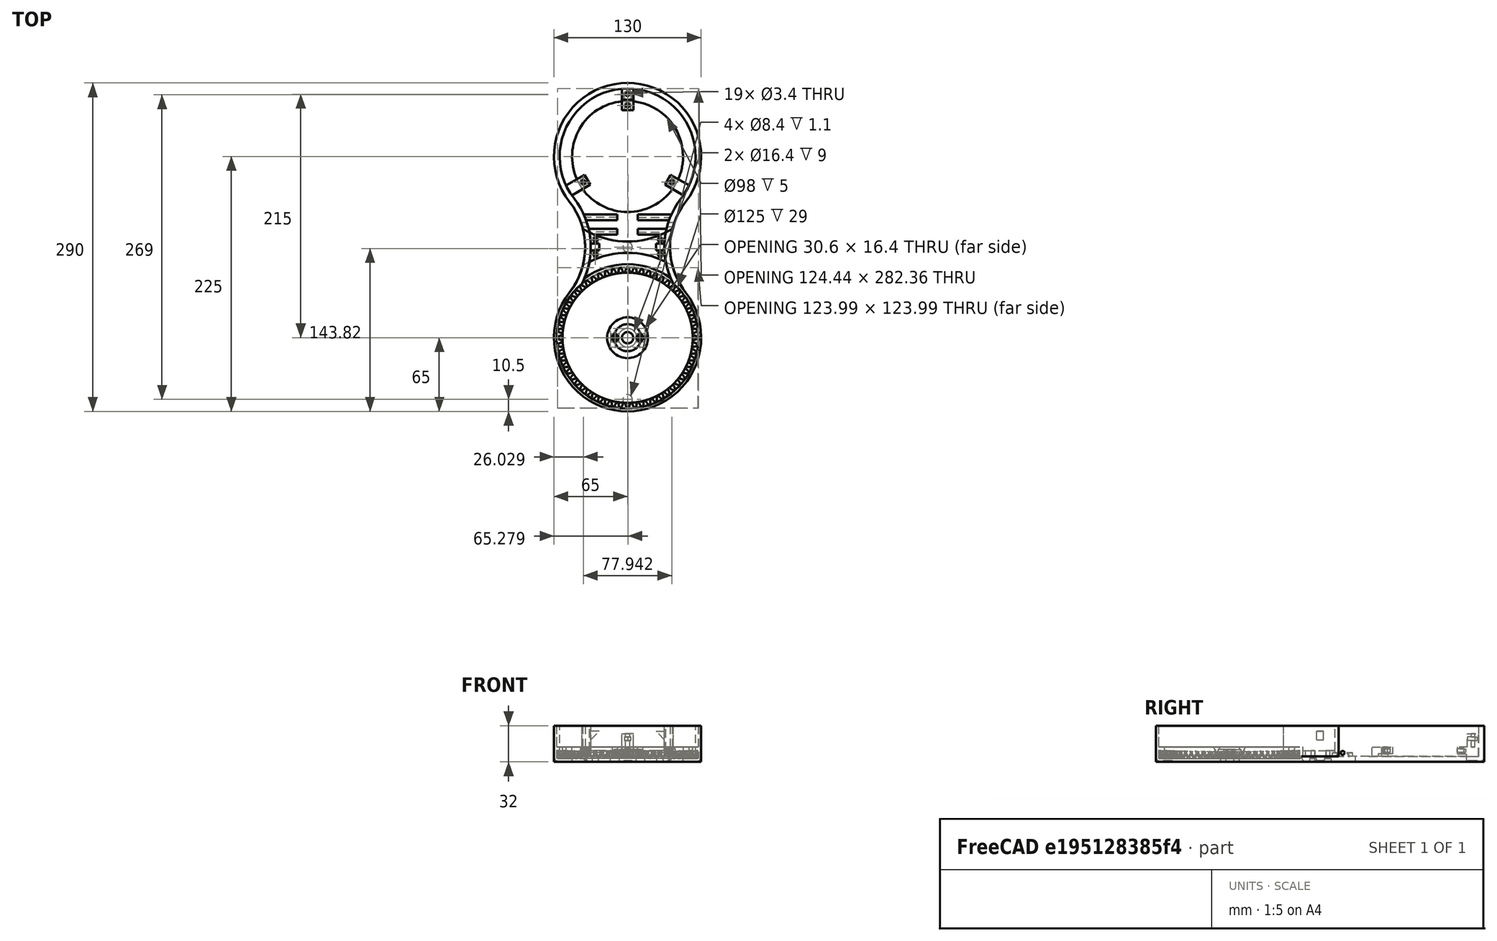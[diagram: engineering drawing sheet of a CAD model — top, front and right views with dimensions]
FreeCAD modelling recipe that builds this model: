
FCSTD DOCUMENT  (FreeCAD 0.19R24276 (Git))
Label: Art2BodyA_Splitted_A
License: All rights reserved
LicenseURL: http://en.wikipedia.org/wiki/All_rights_reserved
objects: Sketcher::SketchObject×25, PartDesign::Pocket×17, PartDesign::Line×11, PartDesign::CoordinateSystem×10, PartDesign::Pad×8, PartDesign::Plane×4, PartDesign::Body×3, PartDesign::FeatureBase×2, Spreadsheet::Sheet×1, Part::FeaturePython×1, Part::Cylinder×1, Part::Cut×1, Part::MultiFuse×1, PartDesign::Chamfer×1, PartDesign::Mirrored×1, PartDesign::PolarPattern×1, PartDesign::Fillet×1, Part::Feature×1
note: 116 computed .brp shape members not serialized (recipe doc carries the construction recipe); baked Part::Feature solids carry a one-line shape summary decoded from their .brp

FEATURE [Spreadsheet::Sheet] Spreadsheet
  cells = A2=M3BoltBodyRadius; B2(M3BoltBodyRadius)=1.7; A3=M3BoltHeadRadius; B3(M3BoltHeadRadius)=2.95; A4=M3NutCircumradius; B4(M3NutCircumradius)=3.35; A5=M3NutThickness; B5(M3NutThickness)=3; A6=Bearing655ZZBodyRadius; B6(Bearing655ZZBodyRadius)=8.199999999999999; A7=MagnetRadius; B7(MagnetRadius)=4.2; A8=MagnetThickness; B8(MagnetThickness)=1.1
FEATURE [Sketcher::SketchObject] Sketch
  FullyConstrained = true
  MapMode = 5
  Support = -> [XY_Plane]
  sketch-geometry (4):
    g0: ArcOfCircle CenterX=0 CenterY=0 CenterZ=0 NormalX=0 NormalY=0 NormalZ=1 AngleXU=0 Radius=65 StartAngle=2.47872 EndAngle=6.94606
    g1: ArcOfCircle CenterX=102.47 CenterY=80 CenterZ=0 NormalX=0 NormalY=0 NormalZ=1 AngleXU=0 Radius=65 StartAngle=2.47872 EndAngle=3.80447
    g2: ArcOfCircle CenterX=-102.47 CenterY=80 CenterZ=0 NormalX=0 NormalY=0 NormalZ=1 AngleXU=0 Radius=65 StartAngle=5.62031 EndAngle=6.94606
    g3: ArcOfCircle CenterX=2.8e-15 CenterY=160 CenterZ=0 NormalX=0 NormalY=0 NormalZ=1 AngleXU=0 Radius=65 StartAngle=5.62031 EndAngle=10.0877
  constraints (10):
    c: Coincident(g0,g-1)
    c: Tangent(g2,g0) = 1.5708
    c: Tangent(g1,g0) = 1.5708
    c: Symmetric(g1,g2,g-2)
    c: Tangent(g3,g1) = 1.5708
    c: Tangent(g3,g2) = 1.5708
    c: Equal(g3,g0)
    c: DistanceY(g0,g3) = 160
    c: Radius(g0) = 65
    c: Equal(g2,g0)
FEATURE [PartDesign::Pad] Pad
  Direction = (1,1,1)
  Length = 32
  Length2 = 100
  Profile = -> Sketch
  Refine = true
  Type = 0
FEATURE [Sketcher::SketchObject] Sketch001
  ExternalGeometry = -> [Pad]
  FullyConstrained = true
  MapMode = 5
  Placement = pos=(0,0,32) rot=(0,0,1;0rad)
  Support = -> [Pad]
  sketch-geometry (4):
    g0: ArcOfCircle CenterX=0 CenterY=0 CenterZ=0 NormalX=0 NormalY=0 NormalZ=1 AngleXU=0 Radius=60 StartAngle=2.47872 EndAngle=6.94606
    g1: ArcOfCircle CenterX=102.47 CenterY=80 CenterZ=0 NormalX=0 NormalY=0 NormalZ=1 AngleXU=0 Radius=70 StartAngle=2.47872 EndAngle=3.80447
    g2: ArcOfCircle CenterX=-102.47 CenterY=80 CenterZ=0 NormalX=0 NormalY=0 NormalZ=1 AngleXU=0 Radius=70 StartAngle=5.62031 EndAngle=6.94606
    g3: ArcOfCircle CenterX=2.7e-15 CenterY=160 CenterZ=0 NormalX=0 NormalY=0 NormalZ=1 AngleXU=0 Radius=60 StartAngle=5.62031 EndAngle=10.0877
  constraints (9):
    c: Coincident(g0,g-1)
    c: Coincident(g1,g-4)
    c: Coincident(g2,g-5)
    c: Coincident(g2,g0)
    c: Coincident(g3,g-3)
    c: Tangent(g3,g2) = 1.5708
    c: Radius(g3) = 60
    c: Tangent(g3,g1) = 1.5708
    c: Tangent(g1,g0) = 1.5708
FEATURE [PartDesign::Pocket] Pocket
  BaseFeature = -> Pad
  Length = 27
  Length2 = 100
  Profile = -> Sketch001
  Refine = true
  Type = 0
FEATURE [Part::FeaturePython] involutegear  # WARN: FeaturePython — macro-defined, semantics opaque (R4)
  Placement = pos=(0,0,3) rot=(0,0,1;0rad)
  backlash = 0
  beta = -32
  clearance = 0.25
  double_helix = false
  dw = 120
  head = 0
  height = 15.5
  module = 2
  numpoints = 6
  pressure_angle = 20
  properties_from_tool = false
  reversed_backlash = false
  shift = 0
  simple = false
  teeth = 60
  transverse_pitch = 6.28319
  undercut = false
  version = 0.0.3
FEATURE [Sketcher::SketchObject] Sketch003
  FullyConstrained = true
  MapMode = 5
  Placement = pos=(0,0,3) rot=(0,0,1;0rad)
  sketch-geometry (1):
    g0: Circle CenterX=0 CenterY=0 CenterZ=0 NormalX=0 NormalY=0 NormalZ=1 AngleXU=0 Radius=18
  constraints (2):
    c: Coincident(g0,g-1)
    c: Radius(g0) = 18
FEATURE [PartDesign::Plane] DatumPlane
  AttachmentOffset = pos=(0,0,9) rot=(0,0,1;0rad)
  Length = 315.452
  MapMode = 5
  Placement = pos=(9,-2e-15,2e-15) rot=(0.57735,0.57735,0.57735;2.0944rad)
  ResizeMode = 0
  Support = -> [YZ_Plane001]
  Width = 82.7027
FEATURE [PartDesign::CoordinateSystem] LCS_Art2BodyA
  AttacherType = Attacher::AttachEngine3D
FEATURE [Part::Cylinder] Cylinder
  Angle = 360
  AttacherType = Attacher::AttachEngine3D
  Height = 13
  Radius = 64.9
FEATURE [Sketcher::SketchObject] Sketch021
  FullyConstrained = true
  MapMode = 5
  Placement = pos=(0,0,32) rot=(0,0,1;0rad)
  Support = -> [Pocket]
  sketch-geometry (1):
    g0: Circle CenterX=0 CenterY=0 CenterZ=0 NormalX=0 NormalY=0 NormalZ=1 AngleXU=0 Radius=62.5
  constraints (2):
    c: Coincident(g0,g-1)
    c: Radius(g0) = 62.5
FEATURE [PartDesign::Pocket] Pocket014
  BaseFeature = -> Pocket
  Length = 29
  Length2 = 100
  Profile = -> Sketch021
  Refine = true
  Type = 0
FEATURE [PartDesign::Body] Body
  Group = -> [Sketch,Pad,Sketch001,Pocket,Sketch021,Pocket014]
  Origin = -> Origin
  Tip = -> Pocket014
FEATURE [PartDesign::Plane] DatumPlane003
  AttachmentOffset = pos=(0,0,-80) rot=(0,0,1;0rad)
  Length = 147.174
  MapMode = 5
  Placement = pos=(0,80,1.78e-14) rot=(1,0,0;1.5708rad)
  ResizeMode = 0
  Support = -> [XZ_Plane001]
  Width = 74.2136
FEATURE [Part::Cut] Cut
  Base = -> Cylinder
  Refine = true
  Tool = -> involutegear
FEATURE [Part::MultiFuse] Fusion
  Refine = true
  Shapes = -> [Cut,Pocket014]
FEATURE [PartDesign::FeatureBase] BaseFeature  label="Fusion001"
  BaseFeature = -> Fusion
FEATURE [PartDesign::Pad] Pad002
  BaseFeature = -> BaseFeature
  Direction = (1,1,1)
  Length = 8
  Length2 = 100
  Profile = -> Sketch003
  Refine = true
  Type = 0
FEATURE [PartDesign::Chamfer] Chamfer
  Angle = 45
  Base = -> Pad002 [Edge755]
  BaseFeature = -> Pad002
  ChamferType = 0
  FlipDirection = false
  Refine = true
  Size = 6
  Size2 = 1
  SupportTransform = false
FEATURE [Sketcher::SketchObject] Sketch004
  FullyConstrained = true
  MapMode = 5
  Placement = pos=(0,0,11) rot=(0,0,1;0rad)
  Support = -> [Chamfer]
  expr: Constraints[5] = Spreadsheet.M3BoltBodyRadius
  sketch-geometry (3):
    g0: Circle CenterX=0 CenterY=0 CenterZ=0 NormalX=0 NormalY=0 NormalZ=1 AngleXU=0 Radius=5
    g1: Circle CenterX=11 CenterY=0 CenterZ=0 NormalX=0 NormalY=0 NormalZ=1 AngleXU=0 Radius=1.7
    g2: Circle CenterX=-11 CenterY=0 CenterZ=0 NormalX=0 NormalY=0 NormalZ=1 AngleXU=0 Radius=1.7
  constraints (7):
    c: Coincident(g0,g-1)
    c: PointOnObject(g1,g-1)
    c: Symmetric(g2,g1,g-2)
    c: DistanceX(g2,g1) = 22
    c: Radius(g0) = 5
    c: Radius(g2) = 1.7
    c: Equal(g1,g2)
FEATURE [PartDesign::Pocket] Pocket001
  BaseFeature = -> Chamfer
  Length = 5
  Length2 = 100
  Profile = -> Sketch004
  Refine = true
  Type = 1
FEATURE [Sketcher::SketchObject] Sketch005
  FullyConstrained = true
  MapMode = 5
  Placement = pos=(0,0,0) rot=(1,0,0;3.14159rad)
  Support = -> [Pocket001]
  expr: Constraints[1] = Spreadsheet.Bearing655ZZBodyRadius
  sketch-geometry (1):
    g0: Circle CenterX=0 CenterY=0 CenterZ=0 NormalX=0 NormalY=0 NormalZ=1 AngleXU=0 Radius=8.2
  constraints (2):
    c: Coincident(g0,g-1)
    c: Radius(g0) = 8.2
FEATURE [PartDesign::Pocket] Pocket002
  BaseFeature = -> Pocket001
  Length = 9
  Length2 = 100
  Profile = -> Sketch005
  Refine = true
  Type = 0
FEATURE [Sketcher::SketchObject] Sketch006
  FullyConstrained = true
  MapMode = 5
  Placement = pos=(0,0,0) rot=(1,0,0;3.14159rad)
  Support = -> [Pocket002]
  sketch-geometry (4):
    g0: LineSegment StartX=-15.3 StartY=3.5 StartZ=0 EndX=15.3 EndY=3.5 EndZ=0
    g1: LineSegment StartX=15.3 StartY=3.5 StartZ=0 EndX=15.3 EndY=-3.5 EndZ=0
    g2: LineSegment StartX=15.3 StartY=-3.5 StartZ=0 EndX=-15.3 EndY=-3.5 EndZ=0
    g3: LineSegment StartX=-15.3 StartY=-3.5 StartZ=0 EndX=-15.3 EndY=3.5 EndZ=0
  constraints (10):
    c: Coincident(g0,g1)
    c: Coincident(g1,g2)
    c: Coincident(g2,g3)
    c: Coincident(g3,g0)
    c: Horizontal(g0)
    c: Vertical(g3)
    c: Symmetric(g0,g1,g-1)
    c: Symmetric(g2,g1,g-2)
    c: DistanceX(g2,g2) = 30.6
    c: DistanceY(g3,g3) = 7
FEATURE [PartDesign::Pocket] Pocket003
  BaseFeature = -> Pocket002
  Length = 4
  Length2 = 100
  Profile = -> Sketch006
  Refine = true
  Type = 0
FEATURE [Sketcher::SketchObject] Sketch007
  ExternalGeometry = -> [Pocket003]
  FullyConstrained = true
  MapMode = 5
  Placement = pos=(0,0,11) rot=(0,0,1;0rad)
  Support = -> [Pocket003]
  expr: Constraints[39] = Spreadsheet.M3NutCircumradius
  sketch-geometry (14):
    g0: LineSegment StartX=11 StartY=3.35 StartZ=0 EndX=8.09881 EndY=1.675 EndZ=0
    g1: LineSegment StartX=8.09881 StartY=1.675 StartZ=0 EndX=8.09881 EndY=-1.675 EndZ=0
    g2: LineSegment StartX=8.09881 StartY=-1.675 StartZ=0 EndX=11 EndY=-3.35 EndZ=0
    g3: LineSegment StartX=11 StartY=-3.35 StartZ=0 EndX=13.9012 EndY=-1.675 EndZ=0
    g4: LineSegment StartX=13.9012 StartY=-1.675 StartZ=0 EndX=13.9012 EndY=1.675 EndZ=0
    g5: LineSegment StartX=13.9012 StartY=1.675 StartZ=0 EndX=11 EndY=3.35 EndZ=0
    g6: Circle CenterX=11 CenterY=0 CenterZ=0 NormalX=0 NormalY=0 NormalZ=1 AngleXU=0 Radius=3.35
    g7: LineSegment StartX=-11 StartY=3.35 StartZ=0 EndX=-13.9012 EndY=1.675 EndZ=0
    g8: LineSegment StartX=-13.9012 StartY=1.675 StartZ=0 EndX=-13.9012 EndY=-1.675 EndZ=0
    g9: LineSegment StartX=-13.9012 StartY=-1.675 StartZ=0 EndX=-11 EndY=-3.35 EndZ=0
    g10: LineSegment StartX=-11 StartY=-3.35 StartZ=0 EndX=-8.09881 EndY=-1.675 EndZ=0
    g11: LineSegment StartX=-8.09881 StartY=-1.675 StartZ=0 EndX=-8.09881 EndY=1.675 EndZ=0
    g12: LineSegment StartX=-8.09881 StartY=1.675 StartZ=0 EndX=-11 EndY=3.35 EndZ=0
    g13: Circle CenterX=-11 CenterY=0 CenterZ=0 NormalX=0 NormalY=0 NormalZ=1 AngleXU=0 Radius=3.35
  constraints (32):
    c: Coincident(g0,g1)
    c: Coincident(g1,g2)
    c: Coincident(g2,g3)
    c: Coincident(g3,g4)
    c: Coincident(g4,g5)
    c: Coincident(g5,g0)
    c: Equal(g0, g1-g5) x5
    c: PointOnObject(g0,g6)
    c: PointOnObject(g1,g6)
    c: PointOnObject(g2,g6)
    c: PointOnObject(g3,g6)
    c: PointOnObject(g4,g6)
    c: PointOnObject(g5,g6)
    c: Coincident(g6,g-3)
    c: Coincident(g7,g8)
    c: Coincident(g8,g9)
    c: Coincident(g9,g10)
    c: Coincident(g10,g11)
    c: Coincident(g11,g12)
    c: Coincident(g12,g7)
    c: Equal(g7, g8-g12) x5
    c: PointOnObject(g7,g13)
    c: PointOnObject(g8,g13)
    c: PointOnObject(g9,g13)
    c: PointOnObject(g10,g13)
    c: PointOnObject(g11,g13)
    c: PointOnObject(g12,g13)
    c: Coincident(g13,g-4)
    c: Vertical(g11)
    c: Vertical(g1)
    c: Equal(g6,g13)
    c: Radius(g6) = 3.35
FEATURE [PartDesign::Pocket] Pocket004
  BaseFeature = -> Pocket003
  Length = 4
  Length2 = 100
  Profile = -> Sketch007
  Refine = true
  Type = 0
FEATURE [Sketcher::SketchObject] Sketch008
  ExternalGeometry = -> [Pocket004]
  FullyConstrained = true
  MapMode = 5
  Placement = pos=(0,0,0) rot=(1,0,0;3.14159rad)
  Support = -> [Pocket004]
  sketch-geometry (1):
    g0: Circle CenterX=0 CenterY=-160 CenterZ=0 NormalX=0 NormalY=0 NormalZ=1 AngleXU=0 Radius=49
  constraints (2):
    c: Radius(g0) = 49
    c: Coincident(g0,g-3)
FEATURE [PartDesign::Pocket] Pocket005
  BaseFeature = -> Pocket004
  Length = 5
  Length2 = 100
  Profile = -> Sketch008
  Refine = true
  Type = 0
FEATURE [Sketcher::SketchObject] Sketch009
  ExternalGeometry = -> [Pocket005]
  FullyConstrained = true
  MapMode = 5
  Placement = pos=(0,0,5) rot=(0,0,1;0rad)
  Support = -> [Pocket005]
  sketch-geometry (4):
    g0: ArcOfCircle CenterX=0 CenterY=0 CenterZ=0 NormalX=0 NormalY=0 NormalZ=1 AngleXU=0 Radius=75 StartAngle=1.10499 EndAngle=2.0366
    g1: ArcOfCircle CenterX=2.7e-15 CenterY=160 CenterZ=0 NormalX=0 NormalY=0 NormalZ=1 AngleXU=0 Radius=75 StartAngle=4.24659 EndAngle=5.17819
    g2: ArcOfCircle CenterX=102.47 CenterY=80 CenterZ=0 NormalX=0 NormalY=0 NormalZ=1 AngleXU=0 Radius=70 StartAngle=2.95493 EndAngle=3.32825
    g3: ArcOfCircle CenterX=-102.47 CenterY=80 CenterZ=0 NormalX=0 NormalY=0 NormalZ=1 AngleXU=0 Radius=70 StartAngle=6.09653 EndAngle=6.46984
  constraints (12):
    c: Coincident(g0,g-1)
    c: Radius(g0) = 75
    c: Coincident(g2,g1)
    c: Coincident(g2,g0)
    c: Coincident(g3,g1)
    c: Coincident(g3,g0)
    c: Equal(g1,g0)
    c: Coincident(g1,g-3)
    c: Equal(g3,g2)
    c: Coincident(g2,g-4)
    c: Coincident(g3,g-5)
    c: Equal(g3,g-5)
FEATURE [PartDesign::Pad] Pad003
  BaseFeature = -> Pocket005
  Direction = (1,1,1)
  Length = 5
  Length2 = 100
  Profile = -> Sketch009
  Refine = true
  Type = 0
FEATURE [Sketcher::SketchObject] Sketch010
  ExternalGeometry = -> [Pad003]
  FullyConstrained = true
  MapMode = 5
  Placement = pos=(9,-2e-15,2e-15) rot=(0.57735,0.57735,0.57735;2.0944rad)
  Support = -> [DatumPlane]
  sketch-geometry (8):
    g0: LineSegment StartX=91 StartY=8.03897 StartZ=0 EndX=96 EndY=8.03897 EndZ=0
    g1: LineSegment StartX=96 StartY=8.03897 StartZ=0 EndX=93.45 EndY=5 EndZ=0
    g2: LineSegment StartX=93.45 StartY=5 StartZ=0 EndX=91 EndY=5 EndZ=0
    g3: LineSegment StartX=91 StartY=5 StartZ=0 EndX=91 EndY=8.03897 EndZ=0
    g4: LineSegment StartX=103.7 StartY=8.03897 StartZ=0 EndX=108.7 EndY=8.03897 EndZ=0
    g5: LineSegment StartX=108.7 StartY=8.03897 StartZ=0 EndX=108.7 EndY=5 EndZ=0
    g6: LineSegment StartX=108.7 StartY=5 StartZ=0 EndX=106.25 EndY=5 EndZ=0
    g7: LineSegment StartX=106.25 StartY=5 StartZ=0 EndX=103.7 EndY=8.03897 EndZ=0
  constraints (24):
    c: Horizontal(g0)
    c: Coincident(g0,g1)
    c: PointOnObject(g1,g-3)
    c: Coincident(g1,g2)
    c: Horizontal(g2)
    c: Coincident(g2,g3)
    c: Vertical(g3)
    c: Coincident(g0,g3)
    c: Horizontal(g4)
    c: Coincident(g4,g5)
    c: Vertical(g5)
    c: Coincident(g5,g6)
    c: Horizontal(g6)
    c: Coincident(g6,g7)
    c: Coincident(g7,g4)
    c: Equal(g1,g7)
    c: Equal(g5,g3)
    c: Equal(g4,g0)
    c: PointOnObject(g6,g-3)
    c: DistanceX(g1,g6) = 12.8
    c: DistanceX(g0,g4) = 7.7
    c: Angle(g-3,g1) = 0.872665
    c: DistanceX(g0,g0) = 5
    c: DistanceX(g-1,g2) = 91
FEATURE [PartDesign::Pad] Pad004
  BaseFeature = -> Pad003
  Direction = (1,1,1)
  Length = 10
  Length2 = 100
  Profile = -> Sketch010
  Refine = true
  Type = 3
  UpToFace = -> Pad003 [Face265]
FEATURE [PartDesign::Mirrored] Mirrored
  BaseFeature = -> Pad004
  MirrorPlane = -> YZ_Plane001
  Originals = -> [Pad004]
  Refine = true
FEATURE [Sketcher::SketchObject] Sketch011
  ExternalGeometry = -> [Mirrored]
  FullyConstrained = true
  MapMode = 5
  Placement = pos=(0,0,0) rot=(0.57735,0.57735,0.57735;2.0944rad)
  Support = -> [YZ_Plane001]
  sketch-geometry (6):
    g0: LineSegment StartX=221 StartY=5 StartZ=0 EndX=221 EndY=13 EndZ=0
    g1: LineSegment StartX=221 StartY=13 StartZ=0 EndX=201 EndY=13 EndZ=0
    g2: LineSegment StartX=201 StartY=13 StartZ=0 EndX=201 EndY=7 EndZ=0
    g3: LineSegment StartX=201 StartY=7 StartZ=0 EndX=209 EndY=7 EndZ=0
    g4: LineSegment StartX=209 StartY=7 StartZ=0 EndX=209 EndY=5 EndZ=0
    g5: LineSegment StartX=209 StartY=5 StartZ=0 EndX=221 EndY=5 EndZ=0
  constraints (17):
    c: Vertical(g0)
    c: Coincident(g0,g1)
    c: Coincident(g1,g2)
    c: Coincident(g2,g3)
    c: Coincident(g3,g4)
    c: Coincident(g4,g5)
    c: Coincident(g5,g0)
    c: Horizontal(g5)
    c: Vertical(g4)
    c: Vertical(g2)
    c: Horizontal(g3)
    c: Horizontal(g1)
    c: DistanceX(g3,g3) = 8
    c: DistanceX(g1,g1) = 20
    c: DistanceY(g2,g2) = 6
    c: DistanceY(g4,g4) = 2
    c: Coincident(g4,g-3)
FEATURE [PartDesign::Pad] Pad005
  BaseFeature = -> Mirrored
  Direction = (1,1,1)
  Length = 10
  Length2 = 100
  Midplane = true
  Profile = -> Sketch011
  Refine = true
  Type = 0
FEATURE [Sketcher::SketchObject] Sketch012
  ExternalGeometry = -> [Pad005]
  FullyConstrained = false
  MapMode = 5
  Placement = pos=(-3.6e-15,2.9e-15,13) rot=(0,0,1;0rad)
  Support = -> [Pad005]
  expr: Constraints[1] = Spreadsheet.M3BoltBodyRadius
  sketch-geometry (1):
    g0: Circle CenterX=0 CenterY=205 CenterZ=0 NormalX=0 NormalY=0 NormalZ=1 AngleXU=0 Radius=1.7
  constraints (2):
    c: PointOnObject(g0,g-2)
    c: Radius(g0) = 1.7
FEATURE [PartDesign::Pocket] Pocket006
  BaseFeature = -> Pad005
  Length = 5
  Length2 = 100
  Profile = -> Sketch012
  Refine = true
  Type = 1
FEATURE [PartDesign::Plane] DatumPlane001
  AttachmentOffset = pos=(0,0,-3) rot=(0,0,1;0rad)
  Length = 168.771
  MapMode = 5
  Placement = pos=(-2.8e-15,2.2e-15,10) rot=(0,0,1;0rad)
  ResizeMode = 0
  Support = -> [Pocket006]
  Width = 328.56
FEATURE [Sketcher::SketchObject] Sketch013
  ExternalGeometry = -> [Pocket006]
  FullyConstrained = true
  MapMode = 5
  Placement = pos=(-2.8e-15,2.2e-15,10) rot=(0,0,1;0rad)
  Support = -> [DatumPlane001]
  expr: Constraints[18] = Spreadsheet.M3NutCircumradius
  sketch-geometry (10):
    g0: LineSegment StartX=0 StartY=208.35 StartZ=0 EndX=-2.90119 EndY=206.675 EndZ=0
    g1: LineSegment StartX=-2.90119 StartY=206.675 StartZ=0 EndX=-2.90119 EndY=203.325 EndZ=0
    g2: LineSegment StartX=-2.90119 StartY=203.325 StartZ=0 EndX=-9.28e-14 EndY=201.65 EndZ=0
    g3: LineSegment StartX=-9.28e-14 StartY=201.65 StartZ=0 EndX=2.90119 EndY=203.325 EndZ=0
    g4: LineSegment StartX=2.90119 StartY=203.325 StartZ=0 EndX=2.90119 EndY=206.675 EndZ=0
    g5: LineSegment StartX=2.90119 StartY=206.675 StartZ=0 EndX=0 EndY=208.35 EndZ=0
    g6: Circle CenterX=0 CenterY=205 CenterZ=0 NormalX=0 NormalY=0 NormalZ=1 AngleXU=0 Radius=3.35
    g7: LineSegment StartX=-2.90119 StartY=206.675 StartZ=0 EndX=-2.90119 EndY=196.675 EndZ=0
    g8: LineSegment StartX=-2.90119 StartY=196.675 StartZ=0 EndX=2.90119 EndY=196.675 EndZ=0
    g9: LineSegment StartX=2.90119 StartY=196.675 StartZ=0 EndX=2.90119 EndY=206.675 EndZ=0
  constraints (24):
    c: Coincident(g0,g1)
    c: Coincident(g1,g2)
    c: Coincident(g2,g3)
    c: Coincident(g3,g4)
    c: Coincident(g4,g5)
    c: Coincident(g5,g0)
    c: Equal(g0, g1-g5) x5
    c: PointOnObject(g0,g6)
    c: PointOnObject(g1,g6)
    c: PointOnObject(g2,g6)
    c: PointOnObject(g3,g6)
    c: PointOnObject(g4,g6)
    c: PointOnObject(g5,g6)
    c: PointOnObject(g5,g-2)
    c: Radius(g6) = 3.35
    c: Coincident(g0,g7)
    c: Vertical(g7)
    c: Coincident(g7,g8)
    c: Horizontal(g8)
    c: Coincident(g8,g9)
    c: Coincident(g9,g5)
    c: Vertical(g9)
    c: DistanceY(g9,g9) = 10
    c: Coincident(g6,g-3)
FEATURE [PartDesign::Pocket] Pocket007
  BaseFeature = -> Pocket006
  Length = 3
  Length2 = 100
  Midplane = true
  Profile = -> Sketch013
  Refine = true
  Type = 0
  expr: Length = Spreadsheet.M3NutThickness
FEATURE [PartDesign::Line] DatumLine
  AttacherType = Attacher::AttachEngineLine
  Length = 20
  MapMode = 19
  Placement = pos=(-7.1e-15,160,0) rot=(-1,0,0;3.14159rad)
  ResizeMode = 0
  Support = -> [Pocket007]
FEATURE [PartDesign::PolarPattern] PolarPattern
  Angle = 360
  Axis = -> DatumLine
  BaseFeature = -> Pocket007
  Occurrences = 3
  Originals = -> [Pad005,Pocket006,Pocket007]
  Refine = true
FEATURE [Sketcher::SketchObject] Sketch014
  ExternalGeometry = -> [PolarPattern]
  FullyConstrained = true
  MapMode = 5
  Placement = pos=(-3.6e-15,2.9e-15,13) rot=(0,0,1;0rad)
  Support = -> [PolarPattern]
  sketch-geometry (4):
    g0: LineSegment StartX=-5 StartY=219.791 StartZ=0 EndX=-5 EndY=210 EndZ=0
    g1: LineSegment StartX=-5 StartY=210 StartZ=0 EndX=5 EndY=210 EndZ=0
    g2: LineSegment StartX=5 StartY=210 StartZ=0 EndX=5 EndY=219.791 EndZ=0
    g3: ArcOfCircle CenterX=1.16e-14 CenterY=160 CenterZ=0 NormalX=0 NormalY=0 NormalZ=1 AngleXU=0 Radius=60 StartAngle=1.48737 EndAngle=1.65423
  constraints (11):
    c: Vertical(g0)
    c: Coincident(g0,g1)
    c: Coincident(g1,g2)
    c: Vertical(g2)
    c: Symmetric(g1,g0,g-2)
    c: Coincident(g3,g0)
    c: Coincident(g3,g2)
    c: DistanceY(g-4,g1) = 9
    c: Coincident(g3,g-3)
    c: Equal(g-3,g3)
    c: DistanceX(g1,g1) = 10
FEATURE [PartDesign::Pad] Pad006
  BaseFeature = -> PolarPattern
  Direction = (1,1,1)
  Length = 12
  Length2 = 100
  Profile = -> Sketch014
  Refine = true
  Type = 0
FEATURE [Sketcher::SketchObject] Sketch015
  ExternalGeometry = -> [Pad006]
  FullyConstrained = true
  MapMode = 5
  Placement = pos=(-7.3e-15,6.8e-15,25) rot=(0,0,1;0rad)
  Support = -> [Pad006]
  expr: Constraints[1] = Spreadsheet.M3BoltBodyRadius
  sketch-geometry (1):
    g0: Circle CenterX=0 CenterY=215 CenterZ=0 NormalX=0 NormalY=0 NormalZ=1 AngleXU=0 Radius=1.7
  constraints (3):
    c: DistanceY(g-3,g0) = 5
    c: Radius(g0) = 1.7
    c: PointOnObject(g0,g-2)
FEATURE [PartDesign::Pocket] Pocket008
  BaseFeature = -> Pad006
  Length = 12
  Length2 = 100
  Profile = -> Sketch015
  Refine = true
  Type = 0
FEATURE [PartDesign::Plane] DatumPlane002
  AttachmentOffset = pos=(0,0,-4.5) rot=(0,0,1;0rad)
  Length = 168.771
  MapMode = 5
  Placement = pos=(-5.9e-15,5.5e-15,20.5) rot=(0,0,1;0rad)
  ResizeMode = 0
  Support = -> [Pocket008]
  Width = 328.56
FEATURE [Sketcher::SketchObject] Sketch016
  ExternalGeometry = -> [Pocket008]
  FullyConstrained = true
  MapMode = 5
  Placement = pos=(-5.9e-15,5.5e-15,20.5) rot=(0,0,1;0rad)
  Support = -> [DatumPlane002]
  expr: Constraints[18] = Spreadsheet.M3NutCircumradius
  sketch-geometry (10):
    g0: LineSegment StartX=0 StartY=211.65 StartZ=0 EndX=2.90119 EndY=213.325 EndZ=0
    g1: LineSegment StartX=2.90119 StartY=213.325 StartZ=0 EndX=2.90119 EndY=216.675 EndZ=0
    g2: LineSegment StartX=2.90119 StartY=216.675 StartZ=0 EndX=6.2e-15 EndY=218.35 EndZ=0
    g3: LineSegment StartX=6.2e-15 StartY=218.35 StartZ=0 EndX=-2.90119 EndY=216.675 EndZ=0
    g4: LineSegment StartX=-2.90119 StartY=216.675 StartZ=0 EndX=-2.90119 EndY=213.325 EndZ=0
    g5: LineSegment StartX=-2.90119 StartY=213.325 StartZ=0 EndX=0 EndY=211.65 EndZ=0
    g6: Circle CenterX=0 CenterY=215 CenterZ=0 NormalX=0 NormalY=0 NormalZ=1 AngleXU=0 Radius=3.35
    g7: LineSegment StartX=2.90119 StartY=216.675 StartZ=0 EndX=2.90119 EndY=206.675 EndZ=0
    g8: LineSegment StartX=2.90119 StartY=206.675 StartZ=0 EndX=-2.90119 EndY=206.675 EndZ=0
    g9: LineSegment StartX=-2.90119 StartY=206.675 StartZ=0 EndX=-2.90119 EndY=216.675 EndZ=0
  constraints (24):
    c: Coincident(g0,g1)
    c: Coincident(g1,g2)
    c: Coincident(g2,g3)
    c: Coincident(g3,g4)
    c: Coincident(g4,g5)
    c: Coincident(g5,g0)
    c: Equal(g0, g1-g5) x5
    c: PointOnObject(g0,g6)
    c: PointOnObject(g1,g6)
    c: PointOnObject(g2,g6)
    c: PointOnObject(g3,g6)
    c: PointOnObject(g4,g6)
    c: PointOnObject(g5,g6)
    c: PointOnObject(g5,g-2)
    c: Radius(g6) = 3.35
    c: Vertical(g7)
    c: Coincident(g7,g8)
    c: Coincident(g8,g9)
    c: Vertical(g9)
    c: Horizontal(g8)
    c: Coincident(g7,g1)
    c: Coincident(g9,g3)
    c: Coincident(g6,g-3)
    c: DistanceY(g7,g7) = 10
FEATURE [PartDesign::Pocket] Pocket009
  BaseFeature = -> Pocket008
  Length = 3
  Length2 = 100
  Midplane = true
  Profile = -> Sketch016
  Refine = true
  Type = 0
  expr: Length = Spreadsheet.M3NutThickness
FEATURE [Sketcher::SketchObject] Sketch017
  ExternalGeometry = -> [Pocket009]
  FullyConstrained = true
  MapMode = 5
  Placement = pos=(0,0,0) rot=(0.57735,0.57735,0.57735;2.0944rad)
  Support = -> [YZ_Plane001]
  expr: Constraints[0] = Spreadsheet.M3BoltBodyRadius
  sketch-geometry (3):
    g0: Circle CenterX=99.85 CenterY=8 CenterZ=0 NormalX=0 NormalY=0 NormalZ=1 AngleXU=0 Radius=1.7
    g1: LineSegment StartX=93.45 StartY=5 StartZ=0 EndX=99.85 EndY=8 EndZ=0
    g2: LineSegment StartX=99.85 StartY=8 StartZ=0 EndX=106.25 EndY=5 EndZ=0
  constraints (7):
    c: Radius(g0) = 1.7
    c: Coincident(g1,g-3)
    c: Coincident(g1,g0)
    c: Coincident(g2,g-4)
    c: Coincident(g0,g2)
    c: Equal(g2,g1)
    c: DistanceY(g1,g0) = 3
FEATURE [PartDesign::Pocket] Pocket010
  BaseFeature = -> Pocket009
  Length = 5
  Length2 = 100
  Midplane = true
  Profile = -> Sketch017
  Refine = true
  Type = 1
FEATURE [Sketcher::SketchObject] Sketch018
  FullyConstrained = true
  MapMode = 5
  Placement = pos=(0,0,0) rot=(1,0,0;3.14159rad)
  Support = -> [Pocket010]
  expr: Constraints[14] = Spreadsheet.M3BoltBodyRadius
  sketch-geometry (8):
    g0: Circle CenterX=-28.5 CenterY=-73.5 CenterZ=0 NormalX=0 NormalY=0 NormalZ=1 AngleXU=0 Radius=1.7
    g1: LineSegment StartX=-28.5 StartY=-73.5 StartZ=0 EndX=28.5 EndY=-73.5 EndZ=0
    g2: LineSegment StartX=28.5 StartY=-73.5 StartZ=0 EndX=28.5 EndY=-86.5 EndZ=0
    g3: LineSegment StartX=28.5 StartY=-86.5 StartZ=0 EndX=-28.5 EndY=-86.5 EndZ=0
    g4: LineSegment StartX=-28.5 StartY=-86.5 StartZ=0 EndX=-28.5 EndY=-73.5 EndZ=0
    g5: Circle CenterX=28.5 CenterY=-73.5 CenterZ=0 NormalX=0 NormalY=0 NormalZ=1 AngleXU=0 Radius=1.7
    g6: Circle CenterX=28.5 CenterY=-86.5 CenterZ=0 NormalX=0 NormalY=0 NormalZ=1 AngleXU=0 Radius=1.7
    g7: Circle CenterX=-28.5 CenterY=-86.5 CenterZ=0 NormalX=0 NormalY=0 NormalZ=1 AngleXU=0 Radius=1.7
  constraints (19):
    c: Coincident(g1,g2)
    c: Coincident(g2,g3)
    c: Coincident(g3,g4)
    c: Coincident(g4,g1)
    c: Horizontal(g1)
    c: Vertical(g2)
    c: Vertical(g4)
    c: Coincident(g1,g0)
    c: Coincident(g5,g1)
    c: Coincident(g6,g2)
    c: Coincident(g7,g3)
    c: Equal(g7,g0)
    c: Equal(g0,g5)
    c: Equal(g5,g6)
    c: Radius(g6) = 1.7
    c: Symmetric(g7,g6,g-2)
    c: DistanceY(g4,g4) = 13
    c: DistanceY(g0,g-1) = 73.5
    c: DistanceX(g3,g3) = 57
FEATURE [PartDesign::Pocket] Pocket011
  BaseFeature = -> Pocket010
  Length = 5
  Length2 = 100
  Profile = -> Sketch018
  Refine = true
  Type = 1
FEATURE [Sketcher::SketchObject] Sketch019
  ExternalGeometry = -> [Pocket011]
  FullyConstrained = true
  MapMode = 5
  Placement = pos=(0,0,0) rot=(1,0,0;3.14159rad)
  Support = -> [Pocket011]
  expr: Constraints[1] = Spreadsheet.M3BoltHeadRadius
  sketch-geometry (4):
    g0: Circle CenterX=-28.5 CenterY=-73.5 CenterZ=0 NormalX=0 NormalY=0 NormalZ=1 AngleXU=0 Radius=2.95
    g1: Circle CenterX=-28.5 CenterY=-86.5 CenterZ=0 NormalX=0 NormalY=0 NormalZ=1 AngleXU=0 Radius=2.95
    g2: Circle CenterX=28.5 CenterY=-73.5 CenterZ=0 NormalX=0 NormalY=0 NormalZ=1 AngleXU=0 Radius=2.95
    g3: Circle CenterX=28.5 CenterY=-86.5 CenterZ=0 NormalX=0 NormalY=0 NormalZ=1 AngleXU=0 Radius=2.95
  constraints (8):
    c: Coincident(g0,g-3)
    c: Radius(g0) = 2.95
    c: Equal(g1,g0)
    c: Coincident(g1,g-4)
    c: Coincident(g2,g-5)
    c: Coincident(g3,g-6)
    c: Equal(g3,g2)
    c: Equal(g2,g0)
FEATURE [PartDesign::Pocket] Pocket012
  BaseFeature = -> Pocket011
  Length = 2.9
  Length2 = 100
  Profile = -> Sketch019
  Refine = true
  Type = 0
FEATURE [PartDesign::Fillet] Fillet
  Base = -> Pocket012 [Edge845,Edge848]
  BaseFeature = -> Pocket012
  Radius = 5
  Refine = true
  SupportTransform = false
FEATURE [Sketcher::SketchObject] Sketch020
  FullyConstrained = true
  MapMode = 5
  Placement = pos=(0,0,0) rot=(1,0,0;3.14159rad)
  Support = -> [Fillet]
  expr: Constraints[8] = Spreadsheet.MagnetRadius
  sketch-geometry (3):
    g0: Circle CenterX=0 CenterY=54.5 CenterZ=0 NormalX=0 NormalY=0 NormalZ=1 AngleXU=0 Radius=4.2
    g1: Circle CenterX=0 CenterY=-80 CenterZ=0 NormalX=0 NormalY=0 NormalZ=1 AngleXU=0 Radius=4.2
    g2: Circle CenterX=0 CenterY=-214.5 CenterZ=0 NormalX=0 NormalY=0 NormalZ=1 AngleXU=0 Radius=4.2
  constraints (9):
    c: PointOnObject(g0,g-2)
    c: PointOnObject(g1,g-2)
    c: PointOnObject(g2,g-2)
    c: DistanceY(g-1,g0) = 54.5
    c: DistanceY(g1,g-1) = 80
    c: DistanceY(g2,g1) = 134.5
    c: Equal(g2,g1)
    c: Equal(g1,g0)
    c: Radius(g2) = 4.2
FEATURE [PartDesign::Pocket] Pocket013
  BaseFeature = -> Fillet
  Length = 1.1
  Length2 = 100
  Profile = -> Sketch020
  Refine = true
  Type = 0
  expr: Length = Spreadsheet.MagnetThickness
FEATURE [PartDesign::CoordinateSystem] LCS_Bearing
  AttacherType = Attacher::AttachEngine3D
  MapMode = 11
  Placement = pos=(0,0,9) rot=(0,0,1;1.5708rad)
  Support = -> [Pocket013]
FEATURE [PartDesign::CoordinateSystem] LCS_Window
  AttacherType = Attacher::AttachEngine3D
  MapMode = 11
  Placement = pos=(-7.1e-15,160,0) rot=(0.707107,-0.707107,0;3.14159rad)
  Support = -> [Pocket013]
FEATURE [PartDesign::CoordinateSystem] LCS_Magnet2  label="LCS_Magnet"
  AttacherType = Attacher::AttachEngine3D
  MapMode = 11
  Placement = pos=(0,214.5,1.1) rot=(0.707107,-0.707107,0;3.14159rad)
  Support = -> [Pocket013]
FEATURE [PartDesign::CoordinateSystem] LCS_Magnet1
  AttacherType = Attacher::AttachEngine3D
  MapMode = 11
  Placement = pos=(0,80,1.1) rot=(0.707107,-0.707107,0;3.14159rad)
  Support = -> [Pocket013]
FEATURE [PartDesign::CoordinateSystem] LCS_Magnet2001  label="LCS_Magnet2"
  AttacherType = Attacher::AttachEngine3D
  MapMode = 11
  Placement = pos=(0,-54.5,1.1) rot=(0.707107,-0.707107,0;3.14159rad)
  Support = -> [Pocket013]
FEATURE [PartDesign::CoordinateSystem] LCS_Tensioner001
  AttacherType = Attacher::AttachEngine3D
  MapMode = 45
  Placement = pos=(-9,99.85,5) rot=(0,0.707107,0.707107;3.14159rad)
  Support = -> [Pocket013]
FEATURE [PartDesign::CoordinateSystem] LCS_Tensioner1
  AttacherType = Attacher::AttachEngine3D
  MapMode = 45
  Placement = pos=(9,99.85,5) rot=(0,0.707107,0.707107;3.14159rad)
  Support = -> [Pocket013]
FEATURE [PartDesign::CoordinateSystem] LCS_BearingFix
  AttacherType = Attacher::AttachEngine3D
  MapMode = 45
  Placement = pos=(9.3e-15,0,4) rot=(0,0,1;1.5708rad)
  Support = -> [Pocket013]
FEATURE [PartDesign::Line] HoleAxis_1
  AttacherType = Attacher::AttachEngineLine
  Length = 4.79083
  MapMode = 19
  Placement = pos=(-3.1e-15,205,11.5) rot=(0,0,1;0rad)
  ResizeMode = 1
  Support = -> [Pocket013]
FEATURE [PartDesign::Line] HoleAxis_2
  AttacherType = Attacher::AttachEngineLine
  Length = 4.79083
  MapMode = 19
  Placement = pos=(-6.4e-15,215,22) rot=(0,0,1;0rad)
  ResizeMode = 1
  Support = -> [Pocket013]
FEATURE [PartDesign::Line] HoleAxis_3
  AttacherType = Attacher::AttachEngineLine
  Length = 4.79858
  MapMode = 19
  Placement = pos=(-38.9711,137.5,11.5) rot=(0,0,1;2.0944rad)
  ResizeMode = 1
  Support = -> [Pocket013]
FEATURE [PartDesign::Line] HoleAxis_4
  AttacherType = Attacher::AttachEngineLine
  Length = 4.79858
  MapMode = 19
  Placement = pos=(38.9711,137.5,11.5) rot=(0,0,1;4.18879rad)
  ResizeMode = 1
  Support = -> [Pocket013]
FEATURE [PartDesign::Line] HoleAxis_5
  AttacherType = Attacher::AttachEngineLine
  Length = 4.79083
  MapMode = 19
  Placement = pos=(-28.5,86.5,2.9) rot=(-1,0,0;3.14159rad)
  ResizeMode = 1
  Support = -> [Pocket013]
FEATURE [PartDesign::Line] HoleAxis_6
  AttacherType = Attacher::AttachEngineLine
  Length = 4.79083
  MapMode = 19
  Placement = pos=(-28.5,73.5,2.9) rot=(-1,0,0;3.14159rad)
  ResizeMode = 1
  Support = -> [Pocket013]
FEATURE [PartDesign::Line] HoleAxis_7
  AttacherType = Attacher::AttachEngineLine
  Length = 4.79083
  MapMode = 19
  Placement = pos=(28.5,73.5,2.9) rot=(-1,0,0;3.14159rad)
  ResizeMode = 1
  Support = -> [Pocket013]
FEATURE [PartDesign::Line] HoleAxis_8
  AttacherType = Attacher::AttachEngineLine
  Length = 4.79083
  MapMode = 19
  Placement = pos=(28.5,86.5,2.9) rot=(-1,0,0;3.14159rad)
  ResizeMode = 1
  Support = -> [Pocket013]
FEATURE [PartDesign::Line] HoleAxis_9
  AttacherType = Attacher::AttachEngineLine
  Length = 4.79083
  MapMode = 19
  Placement = pos=(11,0,7) rot=(0,0,1;0rad)
  ResizeMode = 1
  Support = -> [Pocket013]
FEATURE [PartDesign::Line] HoleAxis_10
  AttacherType = Attacher::AttachEngineLine
  Length = 4.79083
  MapMode = 19
  Placement = pos=(-11,0,7) rot=(0,0,1;0rad)
  ResizeMode = 1
  Support = -> [Pocket013]
FEATURE [PartDesign::CoordinateSystem] LCS_Cover
  AttacherType = Attacher::AttachEngine3D
  AttachmentOffset = pos=(0,0,-32) rot=(0,0,1;0rad)
  MapMode = 11
  Placement = pos=(-7.1e-15,160,32) rot=(0.707107,-0.707107,0;3.14159rad)
  Support = -> [Pocket013]
FEATURE [Sketcher::SketchObject] Sketch022
  ExternalGeometry = -> [Pocket013]
  FullyConstrained = true
  MapMode = 5
  Placement = pos=(0,80,1.78e-14) rot=(1,0,0;1.5708rad)
  Support = -> [DatumPlane003]
  sketch-geometry (6):
    g0: LineSegment StartX=-25 StartY=27 StartZ=0 EndX=-35 EndY=27 EndZ=0
    g1: LineSegment StartX=-35 StartY=27 StartZ=0 EndX=-35 EndY=17 EndZ=0
    g2: LineSegment StartX=-35 StartY=17 StartZ=0 EndX=-25 EndY=27 EndZ=0
    g3: LineSegment StartX=25 StartY=27 StartZ=0 EndX=35 EndY=27 EndZ=0
    g4: LineSegment StartX=35 StartY=27 StartZ=0 EndX=35 EndY=17 EndZ=0
    g5: LineSegment StartX=35 StartY=17 StartZ=0 EndX=25 EndY=27 EndZ=0
  constraints (15):
    c: Horizontal(g0)
    c: Coincident(g0,g1)
    c: Vertical(g1)
    c: Coincident(g1,g2)
    c: Coincident(g2,g0)
    c: Coincident(g3,g4)
    c: Coincident(g4,g5)
    c: Coincident(g5,g3)
    c: Symmetric(g3,g0,g-2)
    c: Symmetric(g0,g3,g-2)
    c: Symmetric(g4,g1,g-2)
    c: DistanceX(g0,g3) = 50
    c: DistanceX(g0,g0) = 10
    c: Angle(g0,g2) = 0.785398
    c: DistanceY(g0,g-3) = 5
FEATURE [PartDesign::Pad] Pad007
  BaseFeature = -> Pocket013
  Direction = (1,1,1)
  Length = 6
  Length2 = 100
  Midplane = true
  Profile = -> Sketch022
  Refine = true
  Type = 0
FEATURE [PartDesign::Body] Body001  label="Art2BodyA"
  BaseFeature = -> Fusion
  Group = -> [BaseFeature,Sketch003,Pad002,Chamfer,Sketch004,Pocket001,Sketch005,Pocket002,Sketch006,Pocket003,Sketch007,Pocket004,Sketch008,Pocket005,Sketch009,Pad003,DatumPlane,Sketch010,Pad004,Mirrored,Sketch011,Pad005,Sketch012,Pocket006,DatumPlane001,Sketch013,Pocket007,DatumLine,PolarPattern,Sketch014,Pad006,Sketch015,Pocket008,DatumPlane002,Sketch016,Pocket009,Sketch017,Pocket010,Sketch018,Pocket011,+28 more]
  Origin = -> Origin001
  Tip = -> Pad007
FEATURE [Part::Feature] Body001001  label="Art2BodyA001"
  shape: bbox 139.7 x 299.7 x 32 mm, 392 faces (baked)
FEATURE [PartDesign::FeatureBase] BaseFeature001
  BaseFeature = -> Body001001
FEATURE [Sketcher::SketchObject] Sketch023
  ExternalGeometry = -> [BaseFeature001]
  FullyConstrained = true
  MapMode = 5
  Placement = pos=(0,0,5) rot=(0,0,1;0rad)
  Support = -> [BaseFeature001]
  sketch-geometry (4):
    g0: ArcOfCircle CenterX=0 CenterY=0 CenterZ=0 NormalX=0 NormalY=0 NormalZ=1 AngleXU=0 Radius=64.9 StartAngle=0.94391 EndAngle=2.19768
    g1: ArcOfCircle CenterX=102.47 CenterY=80 CenterZ=0 NormalX=0 NormalY=0 NormalZ=1 AngleXU=0 Radius=70 StartAngle=3.32825 EndAngle=3.5444
    g2: ArcOfCircle CenterX=-102.47 CenterY=80 CenterZ=0 NormalX=0 NormalY=0 NormalZ=1 AngleXU=0 Radius=70 StartAngle=5.88038 EndAngle=6.09653
    g3: ArcOfCircle CenterX=0 CenterY=0 CenterZ=0 NormalX=0 NormalY=0 NormalZ=1 AngleXU=0 Radius=75 StartAngle=1.10499 EndAngle=2.0366
  constraints (11):
    c: Coincident(g0,g-1)
    c: PointOnObject(g0,g-4)
    c: Coincident(g1,g-4)
    c: Coincident(g1,g0)
    c: Coincident(g2,g-5)
    c: Coincident(g2,g0)
    c: Coincident(g2,g-3)
    c: Coincident(g3,g0)
    c: Coincident(g3,g2)
    c: Coincident(g3,g1)
    c: Equal(g-6,g0)
FEATURE [PartDesign::Pad] Pad008
  BaseFeature = -> BaseFeature001
  Direction = (1,1,1)
  Length = 5
  Length2 = 100
  Profile = -> Sketch023
  Refine = true
  Type = 0
FEATURE [Sketcher::SketchObject] Sketch024
  ExternalGeometry = -> [Pad008]
  FullyConstrained = true
  MapMode = 5
  Placement = pos=(0,0,0) rot=(1,0,0;3.14159rad)
  Support = -> [Pad008]
  sketch-geometry (1):
    g0: Circle CenterX=0 CenterY=-160 CenterZ=0 NormalX=0 NormalY=0 NormalZ=1 AngleXU=0 Radius=75
  constraints (2):
    c: Radius(g0) = 75
    c: Coincident(g-3,g0)
FEATURE [PartDesign::Pocket] Pocket015
  BaseFeature = -> Pad008
  Length = 5
  Length2 = 100
  Profile = -> Sketch024
  Refine = true
  Type = 1
FEATURE [Sketcher::SketchObject] Sketch025
  FullyConstrained = true
  MapMode = 5
  Placement = pos=(0,0,0) rot=(1,0,0;3.14159rad)
  Support = -> [Pocket015]
  sketch-geometry (4):
    g0: ArcOfCircle CenterX=0 CenterY=0 CenterZ=0 NormalX=0 NormalY=0 NormalZ=1 AngleXU=0 Radius=75 StartAngle=3.98266 EndAngle=5.44212
    g1: LineSegment StartX=50 StartY=-55.9017 StartZ=0 EndX=50 EndY=-115.902 EndZ=0
    g2: LineSegment StartX=50 StartY=-115.902 StartZ=0 EndX=-50 EndY=-115.902 EndZ=0
    g3: LineSegment StartX=-50 StartY=-115.902 StartZ=0 EndX=-50 EndY=-55.9017 EndZ=0
  constraints (11):
    c: Coincident(g0,g-1)
    c: Coincident(g1,g2)
    c: Coincident(g2,g3)
    c: Vertical(g1)
    c: Vertical(g3)
    c: Symmetric(g1,g2,g-2)
    c: Coincident(g3,g0)
    c: Coincident(g1,g0)
    c: DistanceX(g2,g2) = 100
    c: DistanceY(g1,g1) = 60
    c: Radius(g0) = 75
FEATURE [PartDesign::Pocket] Pocket016
  BaseFeature = -> Pocket015
  Length = 5
  Length2 = 100
  Profile = -> Sketch025
  Refine = true
  Type = 0
FEATURE [PartDesign::Body] Body001002  label="Art2BodyA_Splitted_A"
  BaseFeature = -> Body001001
  Group = -> [BaseFeature001,Sketch023,Pad008,Sketch024,Pocket015,Sketch025,Pocket016]
  Origin = -> Origin002
  Tip = -> Pocket016
